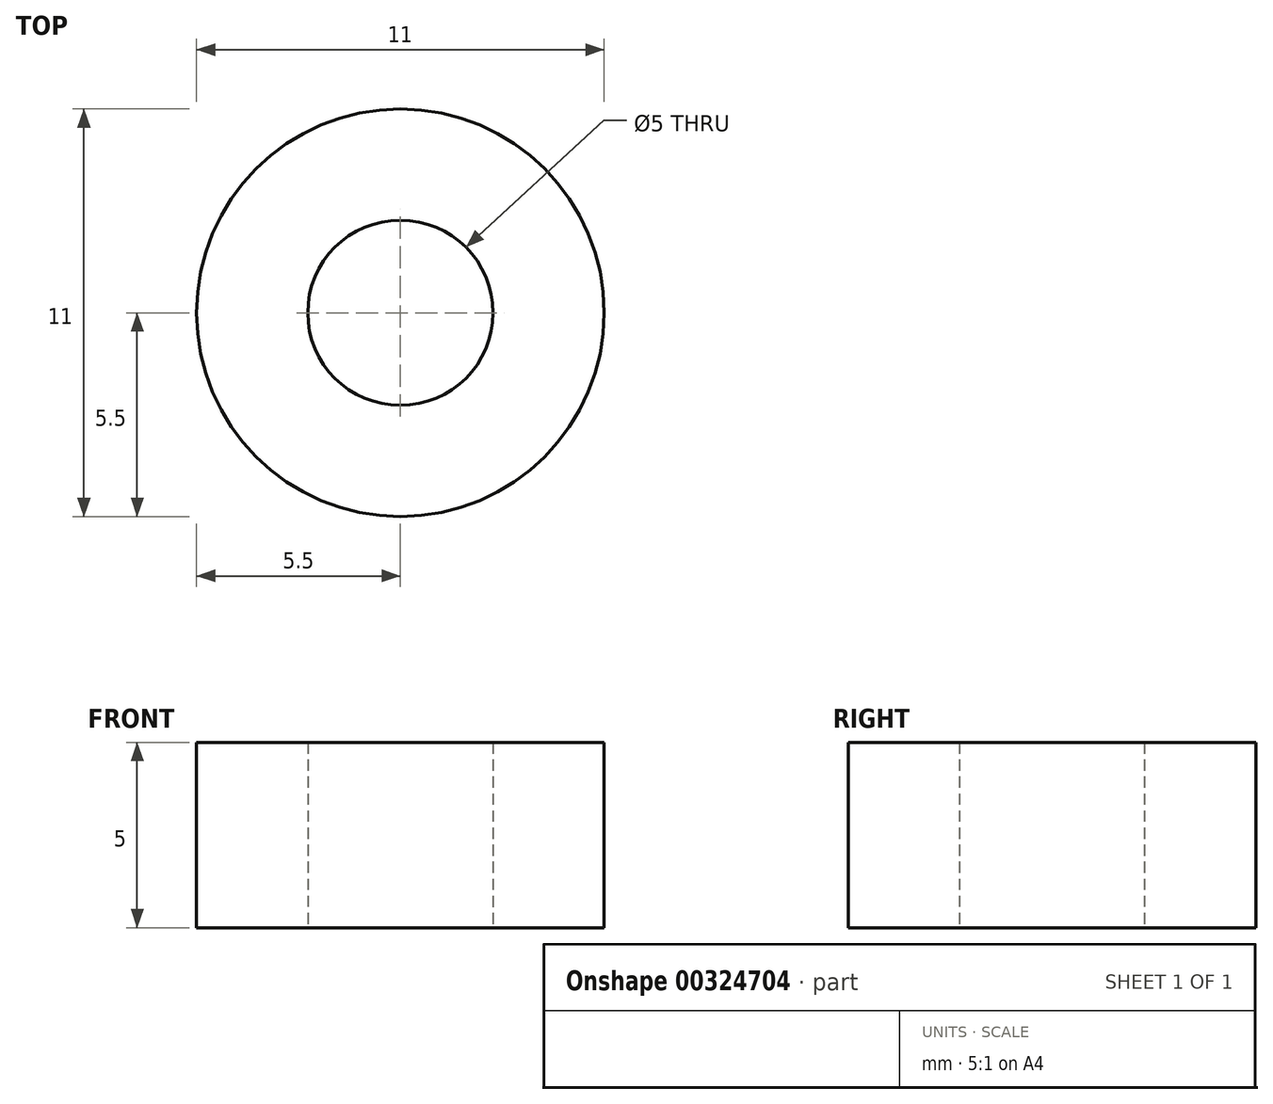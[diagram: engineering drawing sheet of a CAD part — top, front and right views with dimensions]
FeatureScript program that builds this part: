
annotation { "Feature Type Name" : "Feature", "Feature Type Description" : "" }
export const myFeature = defineFeature(function(context is Context, id is Id, definition is map)
    precondition{}
    {
        {
            var Q0;
            Q0=qCreatedBy(makeId("Top.planeOp"),FACE);
            var sketch = newSketch(context, id + "F0", { "sketchPlane" : qUnion([Q0])});
            skCircle(sketch, "E0", {"center": v(0, 0) * mm, "radius": 5.5 * mm});
            skCircle(sketch, "E1", {"center": v(0, 0) * mm, "radius": 2.5 * mm});
            skSolve(sketch);
        }
        {
            var Q0;
            Q0=qSketchRegion(id+"F0",true);
            extrude(context, id + "F1", {"entities" : qUnion([Q0]), "depth" : 5 * mm});
        }
    });
